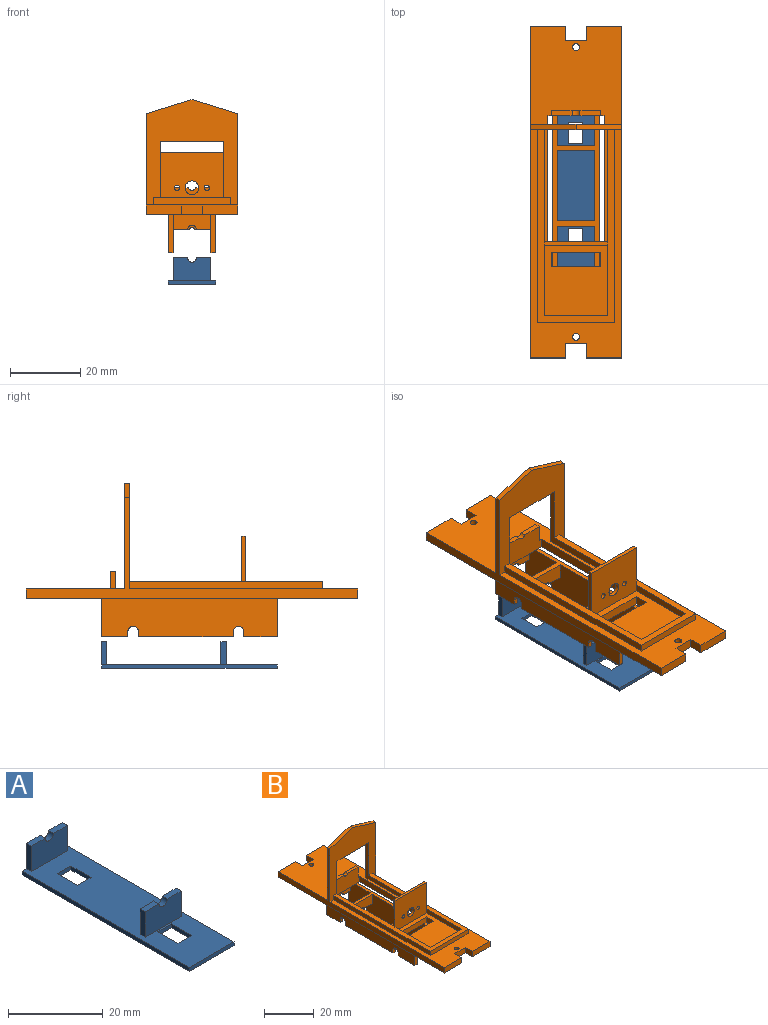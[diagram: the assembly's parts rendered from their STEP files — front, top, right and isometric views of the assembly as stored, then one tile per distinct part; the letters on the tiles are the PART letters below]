
ASSEMBLY  parts=2 mates=1
PART A: 27 faces, bbox 13.4x50x7.6 mm
  f0: plane 10.8x6.55mm, normal (0,1,0), area 68.3mm2, adj f1,f2,f6,f12,f13,f18
  f1: plane 4.15x1.5mm, normal (0,0,1), area 6.2mm2, adj f0,f3,f13,f18
  f2: plane 4.15x1.5mm, normal (0,0,1), area 6.2mm2, adj f0,f3,f12,f18
  f3: plane 10.8x6.55mm, normal (0,-1,0), area 68.3mm2, adj f1,f2,f6,f12,f13,f18
  f4: plane 4.15x1.5mm, normal (0,0,1), area 6.2mm2, adj f9,f15,f16,f17
  f5: plane 4.15x1.5mm, normal (0,0,1), area 6.2mm2, adj f9,f14,f15,f17
  f6: plane 50x13.4mm, normal (0,0,1), area 589.6mm2, adj f0,f3,f7,f8,f9,f10,f12,f13
  f7: plane 13.4x1mm, normal (0,-1,0), area 13.4mm2, adj f6,f8,f10,f11
  f8: plane 50x1mm, normal (-1,0,0), area 50mm2, adj f6,f7,f9,f11
  f9: plane 13.4x7.55mm, normal (0,1,0), area 81.7mm2, adj f4,f5,f6,f8,f10,f11,f14,f16
  f10: plane 50x1mm, normal (1,0,0), area 50mm2, adj f6,f7,f9,f11
  f11: plane 50x13.4mm, normal (0,0,-1), area 622mm2, adj f7,f8,f9,f10,f19,f20,f21,f22
  f12: plane 6.55x1.5mm, normal (1,0,0), area 9.8mm2, adj f0,f2,f3,f6
  f13: plane 6.55x1.5mm, normal (-1,0,0), area 9.8mm2, adj f0,f1,f3,f6
  f14: plane 6.55x1.5mm, normal (1,0,0), area 9.8mm2, adj f5,f6,f9,f15
  f15: plane 10.8x6.55mm, normal (0,-1,0), area 68.3mm2, adj f4,f5,f6,f14,f16,f17
  f16: plane 6.55x1.5mm, normal (-1,0,0), area 9.8mm2, adj f4,f6,f9,f15
  f17: cylinder r=1.25mm len=2.5mm, axis (0,-1,0), area 5.9mm2, adj f4,f5,f9,f15
  f18: cylinder r=1.25mm len=2.5mm, axis (0,-1,0), area 5.9mm2, adj f0,f1,f2,f3
  f19: plane 6x1mm, normal (1,0,0), area 6mm2, adj f6,f11,f20,f21
  f20: plane 4x1mm, normal (0,1,0), area 4mm2, adj f6,f11,f19,f22
  f21: plane 4x1mm, normal (0,-1,0), area 4mm2, adj f6,f11,f19,f22
  f22: plane 6x1mm, normal (-1,0,0), area 6mm2, adj f6,f11,f20,f21
  f23: plane 6x1mm, normal (1,0,0), area 6mm2, adj f6,f11,f24,f25
  f24: plane 4x1mm, normal (0,1,0), area 4mm2, adj f6,f11,f23,f26
  f25: plane 4x1mm, normal (0,-1,0), area 4mm2, adj f6,f11,f23,f26
  f26: plane 6x1mm, normal (-1,0,0), area 6mm2, adj f6,f11,f24,f25
PART B: 97 faces, bbox 26x94.5x43.6 mm
  f0: plane 27x1.3mm, normal (0,0,-1), area 35.1mm2, adj f10,f79,f80,f82
  f1: plane 27x1.3mm, normal (0,0,-1), area 35.1mm2, adj f9,f64,f65,f72
  f2: plane 7.5x1.3mm, normal (0,0,-1), area 9.7mm2, adj f3,f9,f62,f72
  f3: plane 13.4x11mm, normal (0,1,0), area 74.1mm2, adj f2,f9,f10,f13,f71,f72,f82,f83
  f4: plane 10.8x4.45mm, normal (0,-1,0), area 45.5mm2, adj f9,f10,f11,f83,f95,f96
  f5: plane 10.8x4.45mm, normal (0,1,0), area 45.6mm2, adj f9,f10,f70,f89,f93,f94
  f6: plane 10.8x4.45mm, normal (0,-1,0), area 45.6mm2, adj f9,f10,f70,f89,f93,f94
  f7: plane 10.8x4.45mm, normal (0,1,0), area 47.2mm2, adj f9,f10,f70,f90,f91,f92
  f8: plane 10.8x4.45mm, normal (0,-1,0), area 47.2mm2, adj f9,f10,f70,f90,f91,f92
  f9: plane 50x11mm, normal (-1,0,0), area 513.9mm2, adj f1,f2,f3,f4,f5,f6,f7,f8
  f10: plane 50x11mm, normal (1,0,0), area 513.9mm2, adj f0,f3,f4,f5,f6,f7,f8,f11
  f11: plane 10.8x2.5mm, normal (0,0,-1), area 27mm2, adj f4,f9,f10,f14
  f12: plane 61.4x26mm, normal (0,0,1), area 706.7mm2, adj f14,f19,f22,f23,f24,f25,f31,f32
  f13: plane 94.5x26mm, normal (0,0,-1), area 1669.4mm2, adj f3,f9,f10,f14,f22,f23,f24,f25
  f14: plane 16x7.5mm, normal (0,-1,0), area 109.1mm2, adj f11,f12,f13,f15,f55,f56,f70,f84
  f15: plane 5.88x1.5mm, normal (0,0,1), area 8.8mm2, adj f14,f84,f85,f88
  f16: plane 10.8x3.1mm, normal (0,0,-1), area 33.5mm2, adj f9,f10,f49,f53
  f17: plane 20x18mm, normal (0,0,1), area 304mm2, adj f18,f38,f39,f48,f51,f52,f53,f54
  f18: plane 20x2mm, normal (-1,0,0), area 40mm2, adj f17,f38,f43,f48
  f19: plane 33.4x18mm, normal (1,0,0), area 90.8mm2, adj f12,f21,f36,f43,f49,f60
  f20: plane 65x26mm, normal (0,0,1), area 452.9mm2, adj f21,f25,f26,f27,f28,f29,f30,f31
  f21: plane 30x26mm, normal (0,-1,0), area 396mm2, adj f19,f20,f25,f31,f37,f40,f42,f43
  f22: plane 6x2.6mm, normal (0,1,0), area 15.6mm2, adj f12,f13,f23,f35
  f23: plane 4x2.6mm, normal (1,0,0), area 10.4mm2, adj f12,f13,f22,f24
  f24: plane 10x2.6mm, normal (0,1,0), area 26mm2, adj f12,f13,f23,f25
  f25: plane 94.5x28.6mm, normal (-1,0,0), area 284.7mm2, adj f12,f13,f20,f21,f24,f26,f36,f44
  f26: plane 10x2.6mm, normal (0,-1,0), area 26mm2, adj f13,f20,f25,f27
  f27: plane 4x2.6mm, normal (1,0,0), area 10.4mm2, adj f13,f20,f26,f28
  f28: plane 6x2.6mm, normal (0,-1,0), area 15.6mm2, adj f13,f20,f27,f29
  f29: plane 4x2.6mm, normal (-1,0,0), area 10.4mm2, adj f13,f20,f28,f30
  f30: plane 10x2.6mm, normal (0,-1,0), area 26mm2, adj f13,f20,f29,f31
  f31: plane 94.5x28.6mm, normal (1,0,0), area 284.7mm2, adj f12,f13,f20,f21,f30,f32,f36,f45
  f32: plane 10x2.6mm, normal (0,1,0), area 26mm2, adj f12,f13,f31,f35
  f33: cylinder r=1mm len=2.6mm, axis (0,0,-1), area 16.3mm2, adj f12,f13
  f34: cylinder r=1mm len=2.6mm, axis (0,0,-1), area 16.3mm2, adj f13,f20
  f35: plane 4x2.6mm, normal (-1,0,0), area 10.4mm2, adj f12,f13,f22,f32
  f36: plane 30x26mm, normal (0,1,0), area 404mm2, adj f12,f19,f25,f31,f37,f44,f45,f60
  f37: plane 33.4x18mm, normal (-1,0,0), area 90.8mm2, adj f12,f21,f36,f43,f49,f60
  f38: plane 18x2mm, normal (0,1,0), area 36mm2, adj f17,f18,f39,f43
  f39: plane 20x2mm, normal (1,0,0), area 40mm2, adj f17,f38,f43,f48
  f40: plane 55x2mm, normal (-1,0,0), area 110mm2, adj f20,f21,f41,f43
  f41: plane 22x2mm, normal (0,-1,0), area 44mm2, adj f20,f40,f42,f43
  f42: plane 55x2mm, normal (1,0,0), area 110mm2, adj f20,f21,f41,f43
  f43: plane 55x22mm, normal (0,0,1), area 256mm2, adj f18,f19,f21,f37,f38,f39,f40,f41
  f44: plane 13x4mm, normal (-0.29,0,0.96), area 20.4mm2, adj f21,f25,f36,f45
  f45: plane 13x4mm, normal (0.29,0,0.96), area 20.4mm2, adj f21,f31,f36,f44
  f46: plane 13x1.1mm, normal (1,0,0), area 14.3mm2, adj f43,f48,f49,f50
  f47: plane 13x1.1mm, normal (-1,0,0), area 14.3mm2, adj f43,f48,f49,f50
  f48: plane 18x15mm, normal (0,-1,0), area 254.5mm2, adj f17,f18,f39,f46,f47,f50,f57,f58
  f49: plane 18x17.6mm, normal (0,1,0), area 296.1mm2, adj f12,f13,f16,f19,f37,f46,f47,f50
  f50: plane 18x1.1mm, normal (0,0,1), area 19.8mm2, adj f46,f47,f48,f49
  f51: plane 14x2.6mm, normal (0,1,0), area 36.4mm2, adj f13,f17,f52,f54,f61,f73
  f52: plane 4x2.6mm, normal (-1,0,0), area 10.4mm2, adj f13,f17,f51,f53
  f53: plane 14x2.6mm, normal (0,-1,0), area 36.4mm2, adj f13,f16,f17,f52,f54,f61,f73
  f54: plane 4x2.6mm, normal (1,0,0), area 10.4mm2, adj f13,f17,f51,f53
  f55: plane 35.9x2.6mm, normal (-1,0,0), area 93.3mm2, adj f12,f13,f14,f49
  f56: plane 35.9x2.6mm, normal (1,0,0), area 93.3mm2, adj f12,f13,f14,f49
  f57: cylinder r=1.95mm len=3.9mm, axis (0,-1,0), area 13.5mm2, adj f48,f49
  f58: cylinder r=0.75mm len=1.5mm, axis (0,-1,0), area 5.2mm2, adj f48,f49
  f59: cylinder r=0.75mm len=1.5mm, axis (0,-1,0), area 5.2mm2, adj f48,f49
  f60: plane 18x1.5mm, normal (0,0,-1), area 27mm2, adj f19,f21,f36,f37
  f61: plane 4x1.3mm, normal (0,0,1), area 5.2mm2, adj f9,f51,f53,f72
  f62: plane 1.5x1.3mm, normal (0,-1,0), area 2mm2, adj f2,f9,f63,f72
  f63: cylinder r=1.5mm len=3mm, axis (1,0,0), area 6.1mm2, adj f9,f62,f64,f72
  f64: plane 1.5x1.3mm, normal (0,1,0), area 2mm2, adj f1,f9,f63,f72
  f65: plane 1.5x1.3mm, normal (0,-1,0), area 2mm2, adj f1,f9,f66,f72
  f66: cylinder r=1.5mm len=3mm, axis (1,0,0), area 6.1mm2, adj f9,f65,f67,f72
  f67: plane 1.5x1.3mm, normal (0,1,0), area 2mm2, adj f9,f66,f68,f72
  f68: plane 9.5x1.3mm, normal (0,0,-1), area 12.3mm2, adj f9,f67,f69,f72
  f69: plane 11x1.3mm, normal (0,-1,0), area 14.3mm2, adj f9,f13,f68,f72
  f70: plane 35.9x13.4mm, normal (0,0,1), area 125.7mm2, adj f5,f6,f7,f8,f9,f10,f14,f49
  f71: plane 7.5x1.3mm, normal (0,0,-1), area 9.7mm2, adj f3,f10,f74,f82
  f72: plane 50x11mm, normal (1,0,0), area 533.9mm2, adj f1,f2,f3,f13,f61,f62,f63,f64
  f73: plane 4x1.3mm, normal (0,0,1), area 5.2mm2, adj f10,f51,f53,f82
  f74: plane 1.5x1.3mm, normal (0,-1,0), area 2mm2, adj f10,f71,f81,f82
  f75: plane 11x1.3mm, normal (0,-1,0), area 14.3mm2, adj f10,f13,f76,f82
  f76: plane 9.5x1.3mm, normal (0,0,-1), area 12.3mm2, adj f10,f75,f77,f82
  f77: plane 1.5x1.3mm, normal (0,1,0), area 2mm2, adj f10,f76,f78,f82
  f78: cylinder r=1.5mm len=3mm, axis (-1,0,0), area 6.1mm2, adj f10,f77,f79,f82
  f79: plane 1.5x1.3mm, normal (0,-1,0), area 2mm2, adj f0,f10,f78,f82
  f80: plane 1.5x1.3mm, normal (0,1,0), area 2mm2, adj f0,f10,f81,f82
  f81: cylinder r=1.5mm len=3mm, axis (-1,0,0), area 6.1mm2, adj f10,f74,f80,f82
  f82: plane 50x11mm, normal (-1,0,0), area 533.9mm2, adj f0,f3,f13,f70,f71,f73,f74,f75
  f83: cylinder r=1.28mm len=2.55mm, axis (0,1,0), area 6mm2, adj f3,f4,f95,f96
  f84: plane 4.9x1.5mm, normal (1,0,0), area 7.3mm2, adj f12,f14,f15,f85
  f85: plane 14x4.9mm, normal (0,1,0), area 67.5mm2, adj f12,f15,f84,f86,f87,f88
  f86: plane 4.9x1.5mm, normal (-1,0,0), area 7.3mm2, adj f12,f14,f85,f87
  f87: plane 5.88x1.5mm, normal (0,0,1), area 8.8mm2, adj f14,f85,f86,f88
  f88: cylinder r=1.25mm len=2.25mm, axis (0,1,0), area 4.2mm2, adj f14,f15,f85,f87
  f89: cylinder r=1.25mm len=2.5mm, axis (0,-1,0), area 5.9mm2, adj f5,f6,f93,f94
  f90: cylinder r=0.75mm len=1.5mm, axis (0,1,0), area 3.5mm2, adj f7,f8,f91,f92
  f91: plane 4.65x1.5mm, normal (0,0,-1), area 7mm2, adj f7,f8,f10,f90
  f92: plane 4.65x1.5mm, normal (0,0,-1), area 7mm2, adj f7,f8,f9,f90
  f93: plane 4.15x1.5mm, normal (0,0,-1), area 6.2mm2, adj f5,f6,f9,f89
  f94: plane 4.15x1.5mm, normal (0,0,-1), area 6.2mm2, adj f5,f6,f10,f89
  f95: plane 4.13x1.5mm, normal (0,0,-1), area 6.2mm2, adj f3,f4,f10,f83
  f96: plane 4.13x1.5mm, normal (0,0,-1), area 6.2mm2, adj f3,f4,f9,f83
PLACE A t=(0,0,11.62)mm
PLACE B t=(0,0,19.62)mm
MATE fastened A.f9 <-> B.f3  axis (0,1,0) through (5.4,24,10.12)mm
